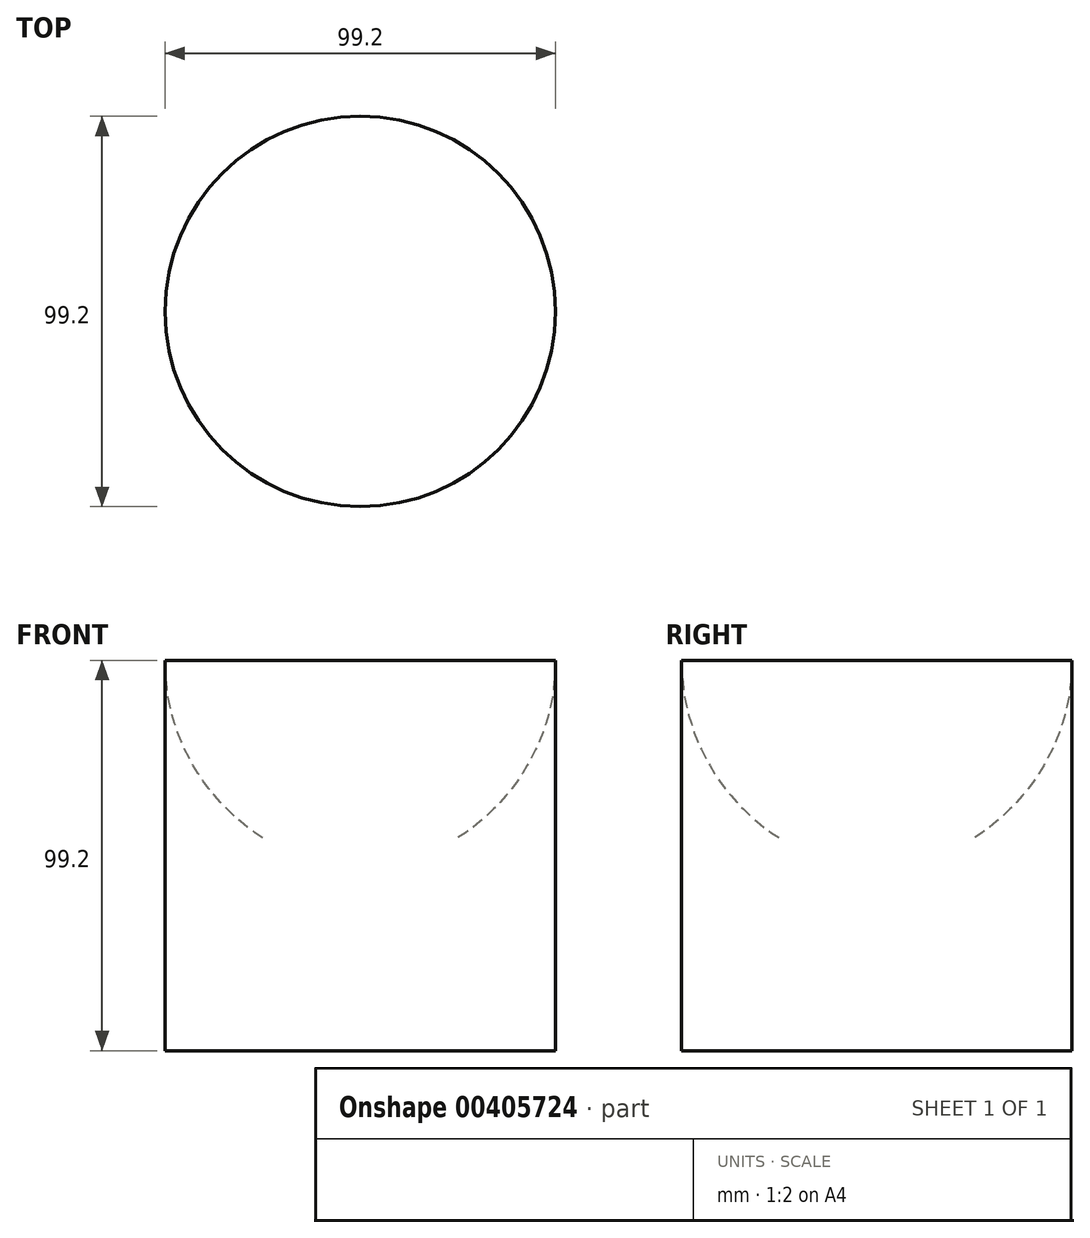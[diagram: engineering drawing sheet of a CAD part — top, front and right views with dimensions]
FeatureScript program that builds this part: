
annotation { "Feature Type Name" : "Feature", "Feature Type Description" : "" }
export const myFeature = defineFeature(function(context is Context, id is Id, definition is map)
    precondition{}
    {
        {
            var Q0;
            Q0=qCreatedBy(makeId("Front.planeOp"),FACE);
            var sketch = newSketch(context, id + "F0", { "sketchPlane" : qUnion([Q0])});
            skLineSegment(sketch, "E0.MirrorCS", {"start": v(49.6, 99.2) * mm, "end": v(49.6, 0) * mm});
            skArc(sketch, "E1.MirrorCS", {"start": v(49.6, 99.2) * mm, "mid": v(43, 73.46) * mm, "end": v(24.8, 54.08) * mm});
            skArc(sketch, "E2.MirrorCS", {"start": v(0, 8.96) * mm, "mid": v(6.6, 34.7) * mm, "end": v(24.8, 54.08) * mm});
            skLineSegment(sketch, "E3.MirrorCS", {"start": v(0, 0) * mm, "end": v(0, 8.96) * mm});
            skLineSegment(sketch, "E4.MirrorCS", {"start": v(0, 0) * mm, "end": v(49.6, 0) * mm});
            skSolve(sketch);
        }
        {
            var Q0;
            Q0=makeQuery(id+"F0.imprint","IMPRINT",FACE,{"disambiguationData":[TD([[makeQuery(id+"F0.imprint","IMPRINT",EDGE,{"derivedFrom":sQuery(id+"F0.wireOp",EDGE,"E0.MirrorCS")}),-1.0]])]});
            var Q1;
            Q1=sQuery(id+"F0.wireOp",EDGE,"E3.MirrorCS");
            revolve(context, id + "F1", {"entities" : qUnion([Q0]), "axis" : qUnion([Q1]), "revolveType" : RevolveType.FULL});
        }
    });
